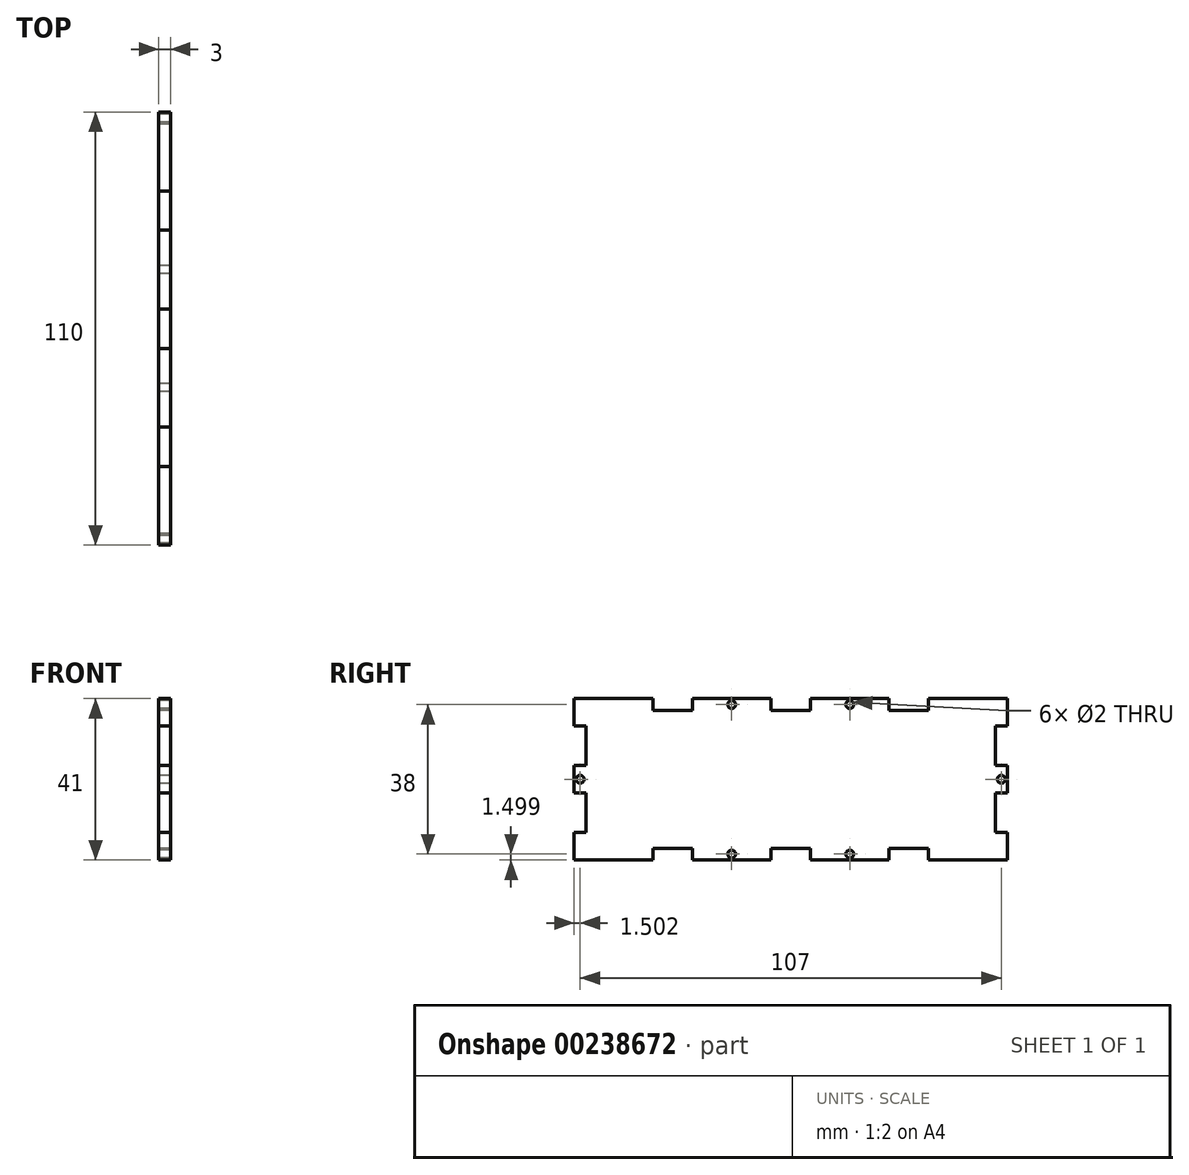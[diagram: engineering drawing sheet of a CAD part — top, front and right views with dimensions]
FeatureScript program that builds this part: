
annotation { "Feature Type Name" : "Feature", "Feature Type Description" : "" }
export const myFeature = defineFeature(function(context is Context, id is Id, definition is map)
    precondition{}
    {
        {
            var Q0;
            Q0=qCreatedBy(makeId("Right.planeOp"),FACE);
            var sketch = newSketch(context, id + "F0", { "sketchPlane" : qUnion([Q0])});
            skLineSegment(sketch, "E0", {"start": v(-98.44, -9.7) * mm, "end": v(-98.44, -2.7) * mm});
            skLineSegment(sketch, "E1", {"start": v(-98.44, -2.7) * mm, "end": v(-95.44, -2.7) * mm});
            skLineSegment(sketch, "E2", {"start": v(-95.44, -2.7) * mm, "end": v(-95.44, 7.3) * mm});
            skLineSegment(sketch, "E3", {"start": v(-95.44, 7.3) * mm, "end": v(-98.44, 7.3) * mm});
            skLineSegment(sketch, "E4", {"start": v(-98.44, 7.3) * mm, "end": v(-98.44, 14.3) * mm});
            skLineSegment(sketch, "E5", {"start": v(-98.44, 14.3) * mm, "end": v(-95.44, 14.3) * mm});
            skLineSegment(sketch, "E6", {"start": v(-95.44, 14.3) * mm, "end": v(-95.44, 24.3) * mm});
            skLineSegment(sketch, "E7", {"start": v(-95.44, 24.3) * mm, "end": v(-98.44, 24.3) * mm});
            skLineSegment(sketch, "E8", {"start": v(-98.44, 24.3) * mm, "end": v(-98.44, 31.3) * mm});
            skLineSegment(sketch, "E9", {"start": v(-98.44, 31.3) * mm, "end": v(-78.44, 31.3) * mm});
            skLineSegment(sketch, "E10", {"start": v(-78.44, 31.3) * mm, "end": v(-78.44, 28.3) * mm});
            skLineSegment(sketch, "E11", {"start": v(-78.44, 28.3) * mm, "end": v(-68.44, 28.3) * mm});
            skLineSegment(sketch, "E12", {"start": v(-68.44, 28.3) * mm, "end": v(-68.44, 31.3) * mm});
            skLineSegment(sketch, "E13", {"start": v(-68.44, 31.3) * mm, "end": v(-48.44, 31.3) * mm});
            skLineSegment(sketch, "E14", {"start": v(-48.44, 28.3) * mm, "end": v(-43.44, 28.3) * mm});
            skLineSegment(sketch, "E15", {"start": v(-48.44, 31.3) * mm, "end": v(-48.44, 28.3) * mm});
            skLineSegment(sketch, "E16", {"start": v(-43.44, 31.23) * mm, "end": v(-43.44, -9.7) * mm, "construction": true});
            skLineSegment(sketch, "E17", {"start": v(-98.44, 10.8) * mm, "end": v(-43.44, 10.8) * mm, "construction": true});
            skCircle(sketch, "E18", {"center": v(-58.44, 29.8) * mm, "radius": 1 * mm});
            skPoint(sketch, "E18.centerSnap0", {"position": v(-58.44, 31.3) * mm});
            skPoint(sketch, "E18.centerSnap1", {"position": v(-48.44, 29.8) * mm});
            skCircle(sketch, "E19", {"center": v(-96.94, 10.8) * mm, "radius": 1 * mm});
            skPoint(sketch, "E19.centerSnap0", {"position": v(-96.94, 14.3) * mm});
            skLineSegment(sketch, "E20.MirrorCS", {"start": v(-78.44, -9.7) * mm, "end": v(-78.44, -6.7) * mm});
            skLineSegment(sketch, "E21.MirrorCS", {"start": v(-48.44, -9.7) * mm, "end": v(-48.44, -6.7) * mm});
            skLineSegment(sketch, "E22.MirrorCS", {"start": v(-68.44, -6.7) * mm, "end": v(-68.44, -9.7) * mm});
            skCircle(sketch, "E23.MirrorC", {"center": v(-58.44, -8.2) * mm, "radius": 1 * mm});
            skLineSegment(sketch, "E24.MirrorCS", {"start": v(-78.44, -6.7) * mm, "end": v(-68.44, -6.7) * mm});
            skLineSegment(sketch, "E25.MirrorCS", {"start": v(-68.44, -9.7) * mm, "end": v(-48.44, -9.7) * mm});
            skPoint(sketch, "E26.MirrorP", {"position": v(-58.44, -9.7) * mm});
            skPoint(sketch, "E27.MirrorP", {"position": v(-48.44, -8.2) * mm});
            skLineSegment(sketch, "E28.MirrorCS", {"start": v(-98.44, -9.7) * mm, "end": v(-78.44, -9.7) * mm});
            skLineSegment(sketch, "E29.MirrorCS", {"start": v(-48.44, -6.7) * mm, "end": v(-43.44, -6.7) * mm});
            skLineSegment(sketch, "E30.MirrorCS", {"start": v(-38.44, 31.3) * mm, "end": v(-38.44, 28.3) * mm});
            skLineSegment(sketch, "E31.MirrorCS", {"start": v(8.56, 24.3) * mm, "end": v(11.56, 24.3) * mm});
            skLineSegment(sketch, "E32.MirrorCS", {"start": v(11.56, 14.3) * mm, "end": v(8.56, 14.3) * mm});
            skLineSegment(sketch, "E33.MirrorCS", {"start": v(11.56, -2.7) * mm, "end": v(8.56, -2.7) * mm});
            skLineSegment(sketch, "E34.MirrorCS", {"start": v(8.56, 7.3) * mm, "end": v(11.56, 7.3) * mm});
            skLineSegment(sketch, "E35.MirrorCS", {"start": v(-8.44, 31.3) * mm, "end": v(-8.44, 28.3) * mm});
            skLineSegment(sketch, "E36.MirrorCS", {"start": v(-18.44, 28.3) * mm, "end": v(-18.44, 31.3) * mm});
            skLineSegment(sketch, "E37.MirrorCS", {"start": v(-38.44, -9.7) * mm, "end": v(-38.44, -6.7) * mm});
            skCircle(sketch, "E38.MirrorC", {"center": v(10.06, 10.8) * mm, "radius": 1 * mm});
            skCircle(sketch, "E39.MirrorC", {"center": v(-28.44, -8.2) * mm, "radius": 1 * mm});
            skCircle(sketch, "E40.MirrorC", {"center": v(-28.44, 29.8) * mm, "radius": 1 * mm});
            skLineSegment(sketch, "E41.MirrorCS", {"start": v(11.56, 7.3) * mm, "end": v(11.56, 14.3) * mm});
            skLineSegment(sketch, "E42.MirrorCS", {"start": v(-18.44, 31.3) * mm, "end": v(-38.44, 31.3) * mm});
            skPoint(sketch, "E43.MirrorP", {"position": v(10.06, 14.3) * mm});
            skLineSegment(sketch, "E44.MirrorCS", {"start": v(-8.44, -6.7) * mm, "end": v(-18.44, -6.7) * mm});
            skLineSegment(sketch, "E45.MirrorCS", {"start": v(11.56, -9.7) * mm, "end": v(-8.44, -9.7) * mm});
            skPoint(sketch, "E46.MirrorP", {"position": v(-28.44, 31.3) * mm});
            skLineSegment(sketch, "E47.MirrorCS", {"start": v(8.56, 14.3) * mm, "end": v(8.56, 24.3) * mm});
            skPoint(sketch, "E48.MirrorP", {"position": v(-38.44, 29.8) * mm});
            skLineSegment(sketch, "E49.MirrorCS", {"start": v(11.56, -9.7) * mm, "end": v(11.56, -2.7) * mm});
            skPoint(sketch, "E50.MirrorP", {"position": v(-28.44, -9.7) * mm});
            skLineSegment(sketch, "E51.MirrorCS", {"start": v(11.56, 24.3) * mm, "end": v(11.56, 31.3) * mm});
            skLineSegment(sketch, "E52.MirrorCS", {"start": v(8.56, -2.7) * mm, "end": v(8.56, 7.3) * mm});
            skLineSegment(sketch, "E53.MirrorCS", {"start": v(11.56, 31.3) * mm, "end": v(-8.44, 31.3) * mm});
            skLineSegment(sketch, "E54.MirrorCS", {"start": v(-8.44, 28.3) * mm, "end": v(-18.44, 28.3) * mm});
            skLineSegment(sketch, "E55.MirrorCS", {"start": v(-18.44, -9.7) * mm, "end": v(-38.44, -9.7) * mm});
            skLineSegment(sketch, "E56.MirrorCS", {"start": v(-18.44, -6.7) * mm, "end": v(-18.44, -9.7) * mm});
            skLineSegment(sketch, "E57.MirrorCS", {"start": v(-8.44, -9.7) * mm, "end": v(-8.44, -6.7) * mm});
            skPoint(sketch, "E58.MirrorP", {"position": v(-38.44, -8.2) * mm});
            skLineSegment(sketch, "E59.MirrorCS", {"start": v(-38.44, -6.7) * mm, "end": v(-43.44, -6.7) * mm});
            skLineSegment(sketch, "E60.MirrorCS", {"start": v(-38.44, 28.3) * mm, "end": v(-43.44, 28.3) * mm});
            skPoint(sketch, "E61.centerSnap0", {"position": v(11.56, 10.8) * mm});
            skPoint(sketch, "E62.centerSnap0", {"position": v(-95.44, 19.3) * mm});
            skPoint(sketch, "E62.centerSnap1", {"position": v(-73.44, 28.3) * mm});
            skPoint(sketch, "E63.centerSnap0", {"position": v(-95.44, 2.3) * mm});
            skPoint(sketch, "E63.centerSnap1", {"position": v(-73.44, -6.7) * mm});
            skSolve(sketch);
        }
        {
            var Q0;
            Q0=qSketchRegion(id+"F0",true);
            extrude(context, id + "F1", {"entities" : qUnion([Q0]), "depth" : 3 * mm});
        }
    });
